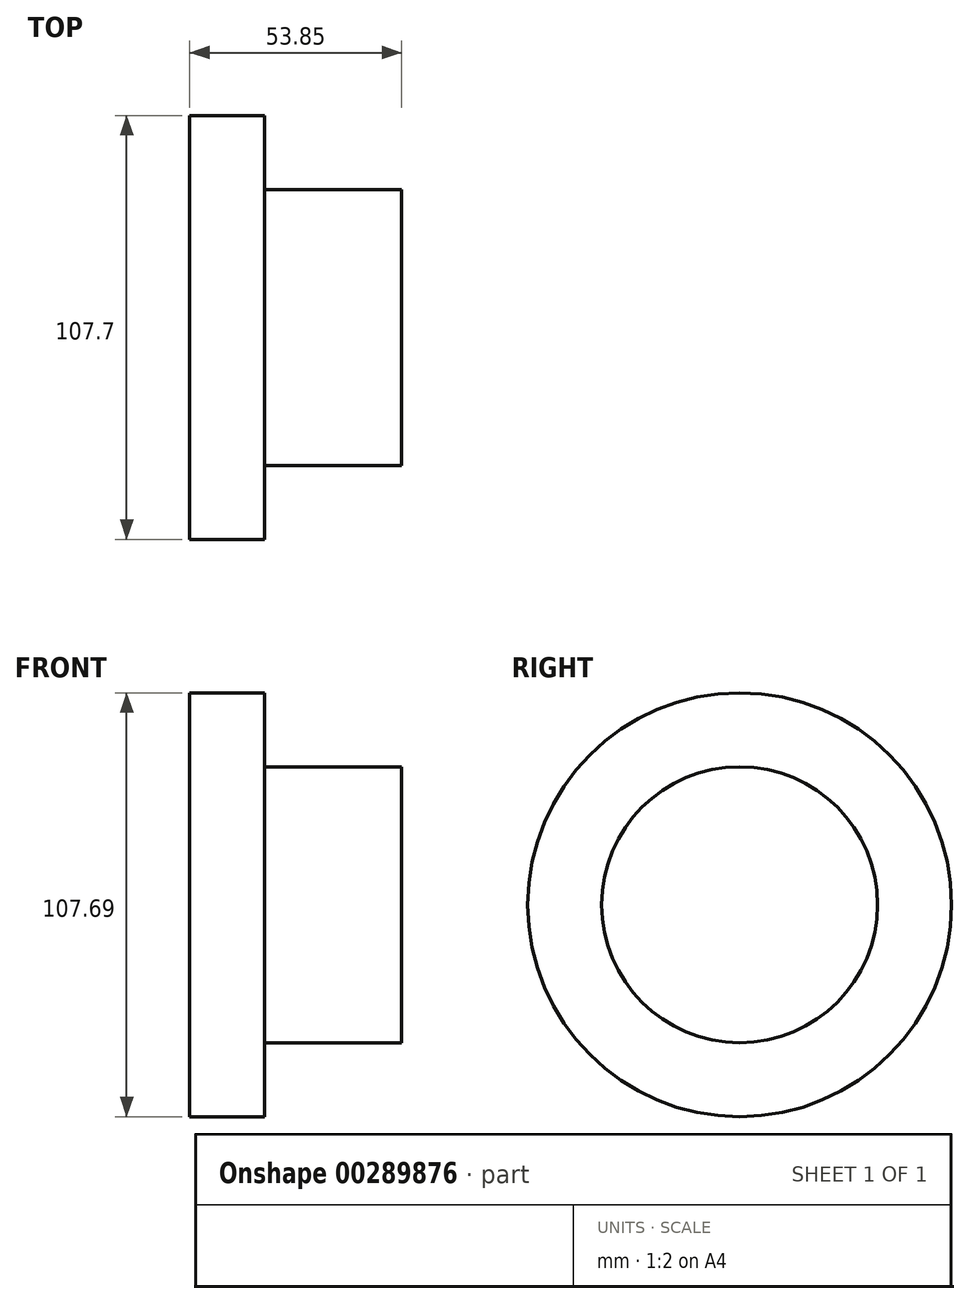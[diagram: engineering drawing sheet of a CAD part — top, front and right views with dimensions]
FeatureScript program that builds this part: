
annotation { "Feature Type Name" : "Feature", "Feature Type Description" : "" }
export const myFeature = defineFeature(function(context is Context, id is Id, definition is map)
    precondition{}
    {
        {
            var Q0;
            Q0=qCreatedBy(makeId("Front.planeOp"),FACE);
            var sketch = newSketch(context, id + "F0", { "sketchPlane" : qUnion([Q0])});
            skLineSegment(sketch, "E0", {"start": v(-18.07, -23.63) * mm, "end": v(-18.07, 30.21) * mm});
            skLineSegment(sketch, "E1", {"start": v(-18.07, 30.21) * mm, "end": v(35.78, 30.21) * mm});
            skLineSegment(sketch, "E2", {"start": v(35.78, 30.21) * mm, "end": v(35.78, -4.84) * mm});
            skLineSegment(sketch, "E3", {"start": v(35.78, -4.84) * mm, "end": v(0.98, -4.84) * mm});
            skLineSegment(sketch, "E4", {"start": v(0.98, -4.84) * mm, "end": v(0.98, -23.63) * mm});
            skLineSegment(sketch, "E5", {"start": v(0.98, -23.63) * mm, "end": v(-18.07, -23.63) * mm});
            skSolve(sketch);
        }
        {
            var Q0;
            Q0=makeQuery(id+"F0.imprint","IMPRINT",FACE,{"disambiguationData":[TD([[makeQuery(id+"F0.imprint","IMPRINT",EDGE,{"derivedFrom":sQuery(id+"F0.wireOp",EDGE,"E0")}),-1.0]])]});
            var Q1;
            Q1=sQuery(id+"F0.wireOp",EDGE,"E1");
            revolve(context, id + "F1", {"entities" : qUnion([Q0]), "axis" : qUnion([Q1]), "revolveType" : RevolveType.FULL});
        }
    });
